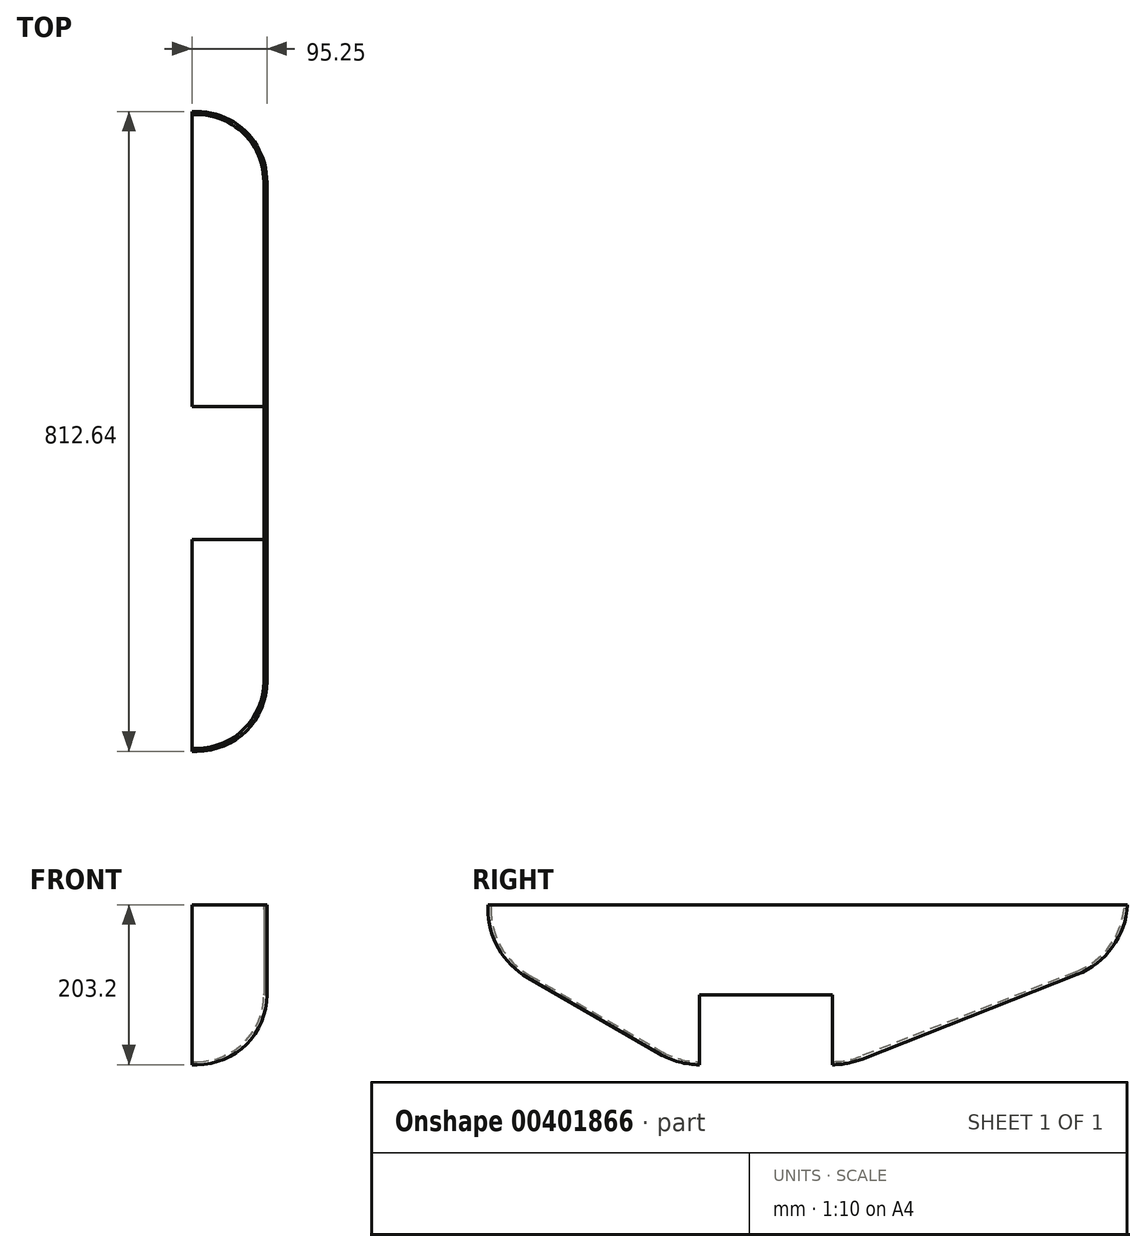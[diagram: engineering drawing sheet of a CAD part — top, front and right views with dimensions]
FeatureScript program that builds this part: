
annotation { "Feature Type Name" : "Feature", "Feature Type Description" : "" }
export const myFeature = defineFeature(function(context is Context, id is Id, definition is map)
    precondition{}
    {
        {
            var Q0;
            Q0=qCreatedBy(makeId("Top.planeOp"),FACE);
            var sketch = newSketch(context, id + "F0", { "sketchPlane" : qUnion([Q0])});
            skLineSegment(sketch, "E0.bottom", {"start": v(95.25, 406.4) * mm, "end": v(-95.25, 406.4) * mm});
            skLineSegment(sketch, "E0.top", {"start": v(95.25, -406.4) * mm, "end": v(-95.25, -406.4) * mm});
            skLineSegment(sketch, "E0.left", {"start": v(95.25, 406.4) * mm, "end": v(95.25, -406.4) * mm});
            skLineSegment(sketch, "E0.right", {"start": v(-95.25, 406.4) * mm, "end": v(-95.25, -406.4) * mm});
            skPoint(sketch, "E0.middle", {"position": v(0, 0) * mm});
            skSolve(sketch);
        }
        {
            var Q0;
            Q0=qSketchRegion(id+"F0",true);
            extrude(context, id + "F1", {"entities" : qUnion([Q0]), "depth" : 406.4 * mm});
        }
        {
            var Q0;
            Q0=makeQuery(id+"F1.opExtrude","CAP_EDGE",EDGE,{"disambiguationData":[OSD([sQuery(id+"F0.wireOp",EDGE,"E0.top")])],"isStart":false});
            var Q1;
            Q1=makeQuery(id+"F1.opExtrude","CAP_EDGE",EDGE,{"disambiguationData":[OSD([sQuery(id+"F0.wireOp",EDGE,"E0.top")])],"isStart":true});
            chamfer(context, id + "F2", {"entities" : qUnion([Q0, Q1]), "chamferType" : ChamferType.OFFSET_ANGLE, "width" : 139.7 * mm, "oppositeDirection" : false, "angle" : 60 * degree, "tangentPropagation" : true});
        }
        {
            var Q0;
            Q0=makeQuery(id+"F1.opExtrude","CAP_EDGE",EDGE,{"disambiguationData":[OSD([sQuery(id+"F0.wireOp",EDGE,"E0.bottom")])],"isStart":false});
            var Q1;
            Q1=makeQuery(id+"F1.opExtrude","CAP_EDGE",EDGE,{"disambiguationData":[OSD([sQuery(id+"F0.wireOp",EDGE,"E0.bottom")])],"isStart":true});
            chamfer(context, id + "F3", {"entities" : qUnion([Q0, Q1]), "chamferType" : ChamferType.TWO_OFFSETS, "width1" : 355.6 * mm, "oppositeDirection" : false, "width2" : 139.7 * mm, "tangentPropagation" : true});
        }
        {
            var Q0;
            {var subQ0=sQuery(id+"F0.wireOp",EDGE,"E0.top");Q0=makeQuery(id+"F2.opChamfer","BLEND_EDGE",EDGE,{"blendedFrom":[makeQuery(id+"F1.opExtrude","CAP_EDGE",EDGE,{"disambiguationData":[OSD([subQ0])],"isStart":false}),makeQuery(id+"F1.opExtrude","SWEPT_FACE",FACE,{"disambiguationData":[OSD([subQ0])]})],"blendedInto":[makeQuery(id+"F1.opExtrude","SWEPT_FACE",FACE,{"disambiguationData":[OSD([subQ0])]})]});}
            var Q1;
            {var subQ0=sQuery(id+"F0.wireOp",EDGE,"E0.top");Q1=makeQuery(id+"F2.opChamfer","BLEND_EDGE",EDGE,{"blendedFrom":[makeQuery(id+"F1.opExtrude","CAP_EDGE",EDGE,{"disambiguationData":[OSD([subQ0])],"isStart":false}),makeQuery(id+"F1.opExtrude","CAP_FACE",FACE,{"disambiguationData":[OSD([sQuery(id+"F0.wireOp",EDGE,"E0.bottom"),subQ0,sQuery(id+"F0.wireOp",EDGE,"E0.left"),sQuery(id+"F0.wireOp",EDGE,"E0.right")])],"isStart":false})],"blendedInto":[makeQuery(id+"F1.opExtrude","CAP_FACE",FACE,{"disambiguationData":[OSD([sQuery(id+"F0.wireOp",EDGE,"E0.bottom"),subQ0,sQuery(id+"F0.wireOp",EDGE,"E0.left"),sQuery(id+"F0.wireOp",EDGE,"E0.right")])],"isStart":false})]});}
            var Q2;
            {var subQ0=sQuery(id+"F0.wireOp",EDGE,"E0.bottom");Q2=makeQuery(id+"F3.opChamfer","BLEND_EDGE",EDGE,{"blendedFrom":[makeQuery(id+"F1.opExtrude","CAP_EDGE",EDGE,{"disambiguationData":[OSD([subQ0])],"isStart":false}),makeQuery(id+"F1.opExtrude","CAP_FACE",FACE,{"disambiguationData":[OSD([subQ0,sQuery(id+"F0.wireOp",EDGE,"E0.top"),sQuery(id+"F0.wireOp",EDGE,"E0.left"),sQuery(id+"F0.wireOp",EDGE,"E0.right")])],"isStart":false})],"blendedInto":[makeQuery(id+"F1.opExtrude","CAP_FACE",FACE,{"disambiguationData":[OSD([subQ0,sQuery(id+"F0.wireOp",EDGE,"E0.top"),sQuery(id+"F0.wireOp",EDGE,"E0.left"),sQuery(id+"F0.wireOp",EDGE,"E0.right")])],"isStart":false})]});}
            var Q3;
            {var subQ0=sQuery(id+"F0.wireOp",EDGE,"E0.bottom");Q3=makeQuery(id+"F3.opChamfer","BLEND_EDGE",EDGE,{"blendedFrom":[makeQuery(id+"F1.opExtrude","CAP_EDGE",EDGE,{"disambiguationData":[OSD([subQ0])],"isStart":false}),makeQuery(id+"F1.opExtrude","SWEPT_FACE",FACE,{"disambiguationData":[OSD([subQ0])]})],"blendedInto":[makeQuery(id+"F1.opExtrude","SWEPT_FACE",FACE,{"disambiguationData":[OSD([subQ0])]})]});}
            var Q4;
            {var subQ0=sQuery(id+"F0.wireOp",EDGE,"E0.bottom");Q4=makeQuery(id+"F3.opChamfer","BLEND_EDGE",EDGE,{"blendedFrom":[makeQuery(id+"F1.opExtrude","CAP_EDGE",EDGE,{"disambiguationData":[OSD([subQ0])],"isStart":true}),makeQuery(id+"F1.opExtrude","SWEPT_FACE",FACE,{"disambiguationData":[OSD([subQ0])]})],"blendedInto":[makeQuery(id+"F1.opExtrude","SWEPT_FACE",FACE,{"disambiguationData":[OSD([subQ0])]})]});}
            var Q5;
            {var subQ0=sQuery(id+"F0.wireOp",EDGE,"E0.bottom");Q5=makeQuery(id+"F3.opChamfer","BLEND_EDGE",EDGE,{"blendedFrom":[makeQuery(id+"F1.opExtrude","CAP_EDGE",EDGE,{"disambiguationData":[OSD([subQ0])],"isStart":true}),makeQuery(id+"F1.opExtrude","CAP_FACE",FACE,{"disambiguationData":[OSD([subQ0,sQuery(id+"F0.wireOp",EDGE,"E0.top"),sQuery(id+"F0.wireOp",EDGE,"E0.left"),sQuery(id+"F0.wireOp",EDGE,"E0.right")])],"isStart":true})],"blendedInto":[makeQuery(id+"F1.opExtrude","CAP_FACE",FACE,{"disambiguationData":[OSD([subQ0,sQuery(id+"F0.wireOp",EDGE,"E0.top"),sQuery(id+"F0.wireOp",EDGE,"E0.left"),sQuery(id+"F0.wireOp",EDGE,"E0.right")])],"isStart":true})]});}
            var Q6;
            {var subQ0=sQuery(id+"F0.wireOp",EDGE,"E0.top");Q6=makeQuery(id+"F2.opChamfer","BLEND_EDGE",EDGE,{"blendedFrom":[makeQuery(id+"F1.opExtrude","CAP_EDGE",EDGE,{"disambiguationData":[OSD([subQ0])],"isStart":true}),makeQuery(id+"F1.opExtrude","CAP_FACE",FACE,{"disambiguationData":[OSD([sQuery(id+"F0.wireOp",EDGE,"E0.bottom"),subQ0,sQuery(id+"F0.wireOp",EDGE,"E0.left"),sQuery(id+"F0.wireOp",EDGE,"E0.right")])],"isStart":true})],"blendedInto":[makeQuery(id+"F1.opExtrude","CAP_FACE",FACE,{"disambiguationData":[OSD([sQuery(id+"F0.wireOp",EDGE,"E0.bottom"),subQ0,sQuery(id+"F0.wireOp",EDGE,"E0.left"),sQuery(id+"F0.wireOp",EDGE,"E0.right")])],"isStart":true})]});}
            var Q7;
            {var subQ0=sQuery(id+"F0.wireOp",EDGE,"E0.top");Q7=makeQuery(id+"F2.opChamfer","BLEND_EDGE",EDGE,{"blendedFrom":[makeQuery(id+"F1.opExtrude","CAP_EDGE",EDGE,{"disambiguationData":[OSD([subQ0])],"isStart":true}),makeQuery(id+"F1.opExtrude","SWEPT_FACE",FACE,{"disambiguationData":[OSD([subQ0])]})],"blendedInto":[makeQuery(id+"F1.opExtrude","SWEPT_FACE",FACE,{"disambiguationData":[OSD([subQ0])]})]});}
            fillet(context, id + "F4", {"entities" : qUnion([Q0, Q1, Q2, Q3, Q4, Q5, Q6, Q7]), "radius" : 101.6 * mm, "tangentPropagation" : true, "allowEdgeOverflow" : false});
        }
        {
            var Q0;
            Q0=makeQuery(id+"F1.opExtrude","SWEPT_FACE",FACE,{"disambiguationData":[OSD([sQuery(id+"F0.wireOp",EDGE,"E0.left")])]});
            var Q1;
            Q1=makeQuery(id+"F1.opExtrude","SWEPT_FACE",FACE,{"disambiguationData":[OSD([sQuery(id+"F0.wireOp",EDGE,"E0.right")])]});
            fillet(context, id + "F5", {"entities" : qUnion([Q0, Q1]), "radius" : 88.9 * mm, "tangentPropagation" : true, "allowEdgeOverflow" : false});
        }
        {
            var Q0;
            {var subQ0=sQuery(id+"F0.wireOp",EDGE,"E0.left");Q0=makeQuery(id+"F5.opFillet","BLEND_FACE",FACE,{"disambiguationData":[OSD([subQ0]),TDD([makeQuery(id+"F1.opExtrude","CAP_EDGE",EDGE,{"disambiguationData":[OSD([subQ0])],"isStart":true})])]});}
            var Q1;
            Q1=makeQuery(id+"F1.opExtrude","CAP_FACE",FACE,{"disambiguationData":[OSD([sQuery(id+"F0.wireOp",EDGE,"E0.bottom"),sQuery(id+"F0.wireOp",EDGE,"E0.top"),sQuery(id+"F0.wireOp",EDGE,"E0.left"),sQuery(id+"F0.wireOp",EDGE,"E0.right")])],"isStart":true});
            var Q2;
            {var subQ0=sQuery(id+"F0.wireOp",EDGE,"E0.right");Q2=makeQuery(id+"F5.opFillet","BLEND_FACE",FACE,{"disambiguationData":[OSD([subQ0]),TDD([makeQuery(id+"F1.opExtrude","CAP_EDGE",EDGE,{"disambiguationData":[OSD([subQ0])],"isStart":true})])]});}
            shell(context, id + "F6", {"entities" : qUnion([Q0, Q1, Q2]), "thickness" : 3.8 * mm});
        }
        {
            var Q0;
            Q0=makeQuery(id+"F1.opExtrude","SWEPT_FACE",FACE,{"disambiguationData":[OSD([sQuery(id+"F0.wireOp",EDGE,"E0.left")])]});
            var sketch = newSketch(context, id + "F7", { "sketchPlane" : qUnion([Q0])});
            skLineSegment(sketch, "E1.bottom", {"start": v(-468.9, 458.17) * mm, "end": v(569.73, 458.17) * mm});
            skLineSegment(sketch, "E1.top", {"start": v(-468.9, 203.2) * mm, "end": v(569.73, 203.2) * mm});
            skLineSegment(sketch, "E1.left", {"start": v(-468.9, 458.17) * mm, "end": v(-468.9, 203.2) * mm});
            skLineSegment(sketch, "E1.right", {"start": v(569.73, 458.17) * mm, "end": v(569.73, 203.2) * mm});
            skFitSpline(sketch, "E2.0", {"points": [v(316.13, 203.2) * mm, v(346.16, 203.2) * mm, v(376.2, 203.2) * mm, v(406.24, 203.2) * mm]});
            skSolve(sketch);
        }
        {
            var Q0;
            Q0=qSketchRegion(id+"F7",true);
            extrude(context, id + "F8", {"entities" : qUnion([Q0]), "operationType" : NewBodyOperationType.REMOVE, "endBound" : BoundingType.THROUGH_ALL, "oppositeDirection" : true, "depth" : 25.4 * mm});
        }
        {
            var Q0;
            {var subQ0=sQuery(id+"F7.wireOp",EDGE,"E1.top");var subQ1=sQuery(id+"F0.wireOp",EDGE,"E0.left");var subQ2=makeQuery(id+"F1.opExtrude","SWEPT_FACE",FACE,{"disambiguationData":[OSD([subQ1])]});var subQ3=subQ2;var subQ6=makeQuery(id+"F7.imprint","INTERSECT",VERTEX,{"derivedFrom":[makeQuery(id+"F5.opFillet","BLEND_EDGE",EDGE,{"blendedFrom":[makeQuery(id+"F1.opExtrude","SWEPT_EDGE",EDGE,{"disambiguationData":[OSD([sQuery(id+"F0.wireOp",EDGE,"E0.top"),subQ1])]}),subQ3],"blendedInto":[subQ3]}),subQ0]});Q0=makeQuery(id+"F8.boolean.opBoolean","COPY",FACE,{"derivedFrom":makeQuery(id+"F8.opExtrude","SWEPT_FACE",FACE,{"disambiguationData":[OSD([subQ0]),TDD([makeQuery(id+"F7.imprint","IMPRINT",EDGE,{"disambiguationData":[TD([[makeQuery(id+"F7.imprint","INTERSECT",VERTEX,{"derivedFrom":[subQ0,sQuery(id+"F7.wireOp",EDGE,"E1.left")]}),-1.0]])],"derivedFrom":subQ0}),makeQuery(id+"F7.imprint","IMPRINT",EDGE,{"disambiguationData":[TD([[subQ6,-1.0]])],"derivedFrom":subQ0})])]})});}
            var sketch = newSketch(context, id + "F9", { "sketchPlane" : qUnion([Q0])});
            skLineSegment(sketch, "E3.bottom", {"start": v(0, 426.55) * mm, "end": v(-196.07, 426.55) * mm});
            skLineSegment(sketch, "E3.top", {"start": v(0, -417.64) * mm, "end": v(-196.07, -417.64) * mm});
            skLineSegment(sketch, "E3.left", {"start": v(0, 426.55) * mm, "end": v(0, -417.64) * mm});
            skLineSegment(sketch, "E3.right", {"start": v(-196.07, 426.55) * mm, "end": v(-196.07, -417.64) * mm});
            skSolve(sketch);
        }
        {
            var Q0;
            Q0 = qSketchRegion(id + "F9", true);
            extrude(context, id + "F10", {"entities" : qUnion([Q0]), "operationType" : NewBodyOperationType.REMOVE, "endBound" : BoundingType.THROUGH_ALL, "oppositeDirection" : true, "depth" : 25.4 * mm});
        }
    });
